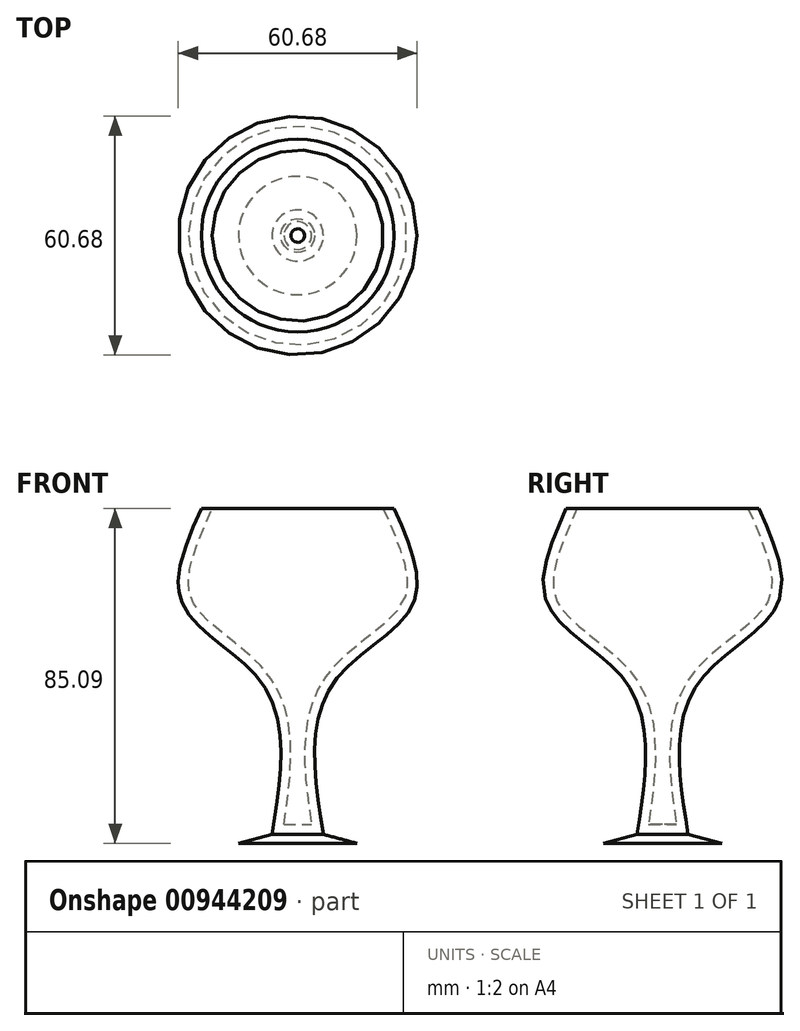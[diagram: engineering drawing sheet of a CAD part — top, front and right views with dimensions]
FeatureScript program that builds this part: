
annotation { "Feature Type Name" : "Feature", "Feature Type Description" : "" }
export const myFeature = defineFeature(function(context is Context, id is Id, definition is map)
    precondition{}
    {
        {
            var Q0;
            Q0=qCreatedBy(makeId("Top.planeOp"),FACE);
            var sketch = newSketch(context, id + "F0", { "sketchPlane" : qUnion([Q0])});
            skCircle(sketch, "E0", {"center": v(0, 0) * mm, "radius": 6.51 * mm});
            skSolve(sketch);
        }
        {
            var Q0;
            Q0=qCreatedBy(makeId("Top.planeOp"),FACE);
            cPlane(context, id + "F1", {"entities" : qUnion([Q0]), "cplaneType" : CPlaneType.OFFSET, "offset" : 82.8 * mm, "width" : 152.4 * mm, "height" : 152.4 * mm});
        }
        {
            var Q0;
            Q0=qCreatedBy(id+"F1.planeOp",FACE);
            var sketch = newSketch(context, id + "F2", { "sketchPlane" : qUnion([Q0])});
            skCircle(sketch, "E1", {"center": v(0, 0) * mm, "radius": 24.48 * mm});
            skSolve(sketch);
        }
        {
            var Q0;
            Q0=qCreatedBy(makeId("Top.planeOp"),FACE);
            cPlane(context, id + "F3", {"entities" : qUnion([Q0]), "cplaneType" : CPlaneType.OFFSET, "offset" : 39.88 * mm, "width" : 152.4 * mm, "height" : 152.4 * mm});
        }
        {
            var Q0;
            Q0=qCreatedBy(makeId("Top.planeOp"),FACE);
            cPlane(context, id + "F4", {"entities" : qUnion([Q0]), "cplaneType" : CPlaneType.OFFSET, "offset" : 59.18 * mm, "width" : 152.4 * mm, "height" : 152.4 * mm});
        }
        {
            var Q0;
            Q0=qCreatedBy(id+"F4.planeOp",FACE);
            var sketch = newSketch(context, id + "F5", { "sketchPlane" : qUnion([Q0])});
            skCircle(sketch, "E2", {"center": v(0, 0) * mm, "radius": 29.54 * mm});
            skSolve(sketch);
        }
        {
            var Q0;
            Q0=qCreatedBy(id+"F3.planeOp",FACE);
            var sketch = newSketch(context, id + "F6", { "sketchPlane" : qUnion([Q0])});
            skCircle(sketch, "E3", {"center": v(0, 0) * mm, "radius": 10.18 * mm});
            skSolve(sketch);
        }
        {
            var Q0;
            Q0=makeQuery(id+"F0.imprint","IMPRINT",FACE,{"disambiguationData":[TD([[makeQuery(id+"F0.imprint","IMPRINT",EDGE,{"derivedFrom":sQuery(id+"F0.wireOp",EDGE,"E0")}),1.0]])]});
            var Q1;
            Q1=makeQuery(id+"F6.imprint","IMPRINT",FACE,{"disambiguationData":[TD([[makeQuery(id+"F6.imprint","IMPRINT",EDGE,{"derivedFrom":sQuery(id+"F6.wireOp",EDGE,"E3")}),1.0]])]});
            var Q2;
            Q2=makeQuery(id+"F5.imprint","IMPRINT",FACE,{"disambiguationData":[TD([[makeQuery(id+"F5.imprint","IMPRINT",EDGE,{"derivedFrom":sQuery(id+"F5.wireOp",EDGE,"E2")}),1.0]])]});
            var Q3;
            Q3=makeQuery(id+"F2.imprint","IMPRINT",FACE,{"disambiguationData":[TD([[makeQuery(id+"F2.imprint","IMPRINT",EDGE,{"derivedFrom":sQuery(id+"F2.wireOp",EDGE,"E1")}),1.0]])]});
            loft(context, id + "F7", {"sheetProfilesArray" : [{ "sheetProfileEntities" : qUnion([Q0]) }, { "sheetProfileEntities" : qUnion([Q1]) }, { "sheetProfileEntities" : qUnion([Q2]) }, { "sheetProfileEntities" : qUnion([Q3]) }]});
        }
        {
            var Q0;
            Q0=makeQuery(id+"F7.opLoft","CAP_FACE",FACE,{"disambiguationData":[OSD([makeQuery(id+"F2.imprint","IMPRINT",FACE,{"disambiguationData":[TD([[makeQuery(id+"F2.imprint","IMPRINT",EDGE,{"derivedFrom":sQuery(id+"F2.wireOp",EDGE,"E1")}),1.0]])]})])],"isStart":true});
            shell(context, id + "F8", {"entities" : qUnion([Q0]), "thickness" : 2.54 * mm});
        }
        {
            var Q0;
            Q0=makeQuery(id+"F7.opLoft","CAP_FACE",FACE,{"disambiguationData":[OSD([makeQuery(id+"F0.imprint","IMPRINT",FACE,{"disambiguationData":[TD([[makeQuery(id+"F0.imprint","IMPRINT",EDGE,{"derivedFrom":sQuery(id+"F0.wireOp",EDGE,"E0")}),1.0]])]})])],"isStart":true});
            extrude(context, id + "F9", {"entities" : qUnion([Q0]), "depth" : 2.3 * mm, "offsetDistance" : 25.4 * mm, "hasDraft" : true, "draftAngle" : 75 * degree});
        }
    });
